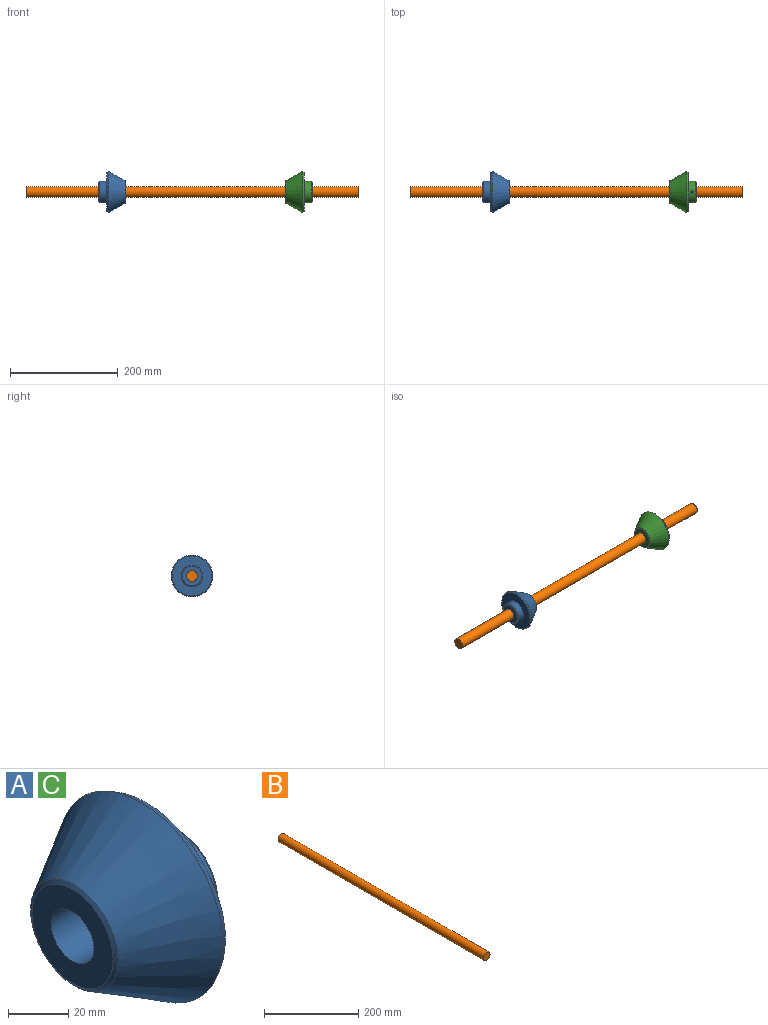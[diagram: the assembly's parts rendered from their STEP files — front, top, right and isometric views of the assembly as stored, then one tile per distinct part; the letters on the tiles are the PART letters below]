
ASSEMBLY  parts=3 mates=4
PART A: 10 faces, bbox 49.6x77x77 mm
  f0: cylinder r=20mm len=40mm, axis (-1,0,0), area 1653.4mm2, adj f2,f6,f9
  f1: cylinder r=10mm len=49.64mm, axis (1,0,0), area 3105.2mm2, adj f4,f5,f9
  f2: plane 74x74mm, normal (1,0,0), area 3044.2mm2, adj f0,f7
  f3: cone r=40mm half-angle=30deg, axis (1,0,0), area 6672.7mm2, adj f7,f8
  f4: plane 38x38mm, normal (-1,0,0), area 820mm2, adj f1,f8
  f5: plane 36.54x36.54mm, normal (1,0,0), area 734.2mm2, adj f1,f6
  f6: cone r=20mm half-angle=45deg, axis (-1,0,0), area 294.5mm2, adj f0,f5
  f7: cone r=38.5mm half-angle=30deg, axis (-1,0,0), area 711.6mm2, adj f2,f3
  f8: cone r=19mm half-angle=60deg, axis (1,0,0), area 214.9mm2, adj f3,f4
  f9: cylinder r=2.1mm len=10.22mm, axis (0,0,1), area 132.7mm2, adj f0,f1
PART B: 3 faces, bbox 20x615x20 mm
  f0: cylinder r=10mm len=615mm, axis (0,1,0), area 38641.6mm2, adj f1,f2
  f1: plane 20x20mm, normal (0,-1,0), area 314.2mm2, adj f0
  f2: plane 20x20mm, normal (0,1,0), area 314.2mm2, adj f0
PART C: same geometry as A
PLACE A rot(axis=(0,1,0),180deg) t=(-172.5,0,0)mm
PLACE B rot(axis=(0.58,0.58,-0.58),120deg) t=(0,0,0)mm
PLACE C t=(222.5,0,0)mm
MATE cylindrical B.f0 <-> C.f0  axis (1,0,0) through (0,0,0)mm
MATE planar A.f0 <-> B.f0  axis (-1,0,0) through (-157.5,0,0)mm
MATE planar C.f0 <-> B.f0  axis (1,0,0) through (207.5,0,0)mm
MATE cylindrical A.f0 <-> B.f0  axis (-1,0,0) through (-172.5,0,0)mm
